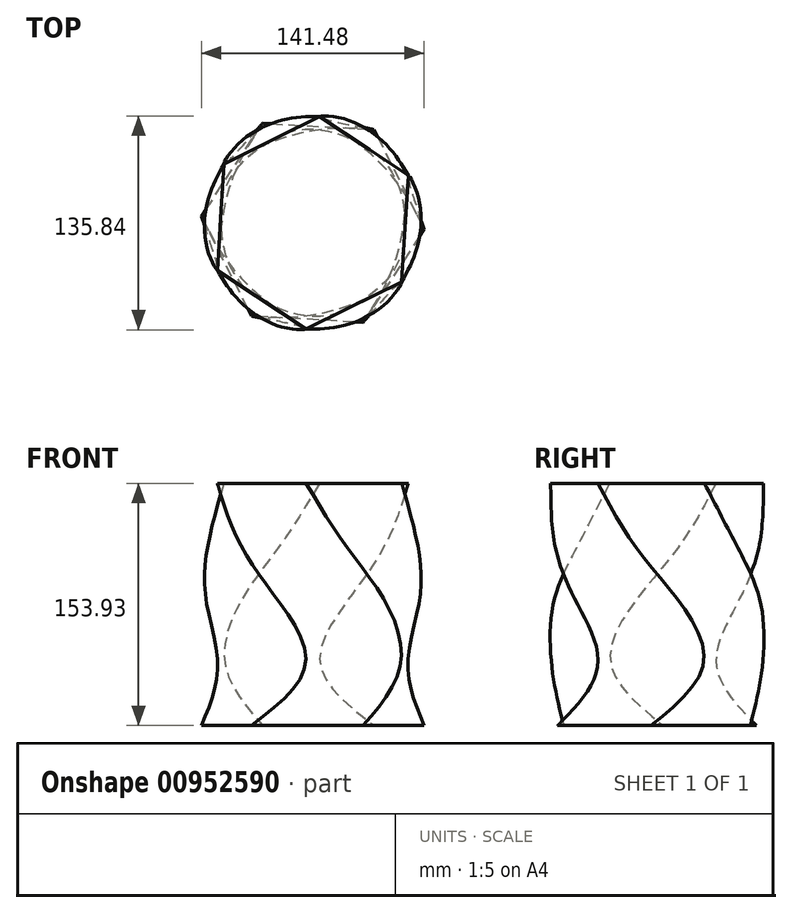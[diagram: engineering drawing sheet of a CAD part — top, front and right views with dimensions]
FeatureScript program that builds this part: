
annotation { "Feature Type Name" : "Feature", "Feature Type Description" : "" }
export const myFeature = defineFeature(function(context is Context, id is Id, definition is map)
    precondition{}
    {
        {
            var Q0;
            Q0=qCreatedBy(makeId("Top.planeOp"),FACE);
            cPlane(context, id + "F0", {"entities" : qUnion([Q0]), "cplaneType" : CPlaneType.OFFSET, "offset" : 77.22 * mm, "width" : 152.4 * mm, "height" : 152.4 * mm});
        }
        {
            var Q0;
            Q0=qCreatedBy(makeId("Top.planeOp"),FACE);
            cPlane(context, id + "F1", {"entities" : qUnion([Q0]), "cplaneType" : CPlaneType.OFFSET, "offset" : 38.1 * mm, "width" : 152.4 * mm, "height" : 152.4 * mm});
        }
        {
            var Q0;
            Q0=qCreatedBy(makeId("Top.planeOp"),FACE);
            cPlane(context, id + "F2", {"entities" : qUnion([Q0]), "cplaneType" : CPlaneType.OFFSET, "offset" : 76.7 * mm, "oppositeDirection" : true, "width" : 152.4 * mm, "height" : 152.4 * mm});
        }
        {
            var Q0;
            Q0=qCreatedBy(makeId("Top.planeOp"),FACE);
            cPlane(context, id + "F3", {"entities" : qUnion([Q0]), "cplaneType" : CPlaneType.OFFSET, "offset" : 34.54 * mm, "oppositeDirection" : true, "width" : 152.4 * mm, "height" : 152.4 * mm});
        }
        {
            var Q0;
            Q0=qCreatedBy(id+"F0.planeOp",FACE);
            var sketch = newSketch(context, id + "F4", { "sketchPlane" : qUnion([Q0])});
            skCircle(sketch, "E0.cCircle", {"center": v(0, 0) * mm, "radius": 58.65 * mm, "construction": true});
            skLineSegment(sketch, "E0.0", {"start": v(-56.43, 37.44) * mm, "end": v(4.21, 67.6) * mm});
            skLineSegment(sketch, "E0.1", {"start": v(4.21, 67.6) * mm, "end": v(60.64, 30.15) * mm});
            skLineSegment(sketch, "E0.2", {"start": v(60.64, 30.15) * mm, "end": v(56.43, -37.44) * mm});
            skLineSegment(sketch, "E0.3", {"start": v(56.43, -37.44) * mm, "end": v(-4.21, -67.6) * mm});
            skLineSegment(sketch, "E0.4", {"start": v(-4.21, -67.6) * mm, "end": v(-60.64, -30.15) * mm});
            skLineSegment(sketch, "E0.5", {"start": v(-60.64, -30.15) * mm, "end": v(-56.43, 37.44) * mm});
            skPoint(sketch, "E0.0.midPoint", {"position": v(-26.11, 52.52) * mm});
            skSolve(sketch);
        }
        {
            var Q0;
            Q0=qCreatedBy(id+"F1.planeOp",FACE);
            var sketch = newSketch(context, id + "F5", { "sketchPlane" : qUnion([Q0])});
            skCircle(sketch, "E1.cCircle", {"center": v(0, 0) * mm, "radius": 59.02 * mm, "construction": true});
            skLineSegment(sketch, "E1.0", {"start": v(45.97, 50.32) * mm, "end": v(66.56, -14.65) * mm});
            skLineSegment(sketch, "E1.1", {"start": v(66.56, -14.65) * mm, "end": v(20.6, -64.97) * mm});
            skLineSegment(sketch, "E1.2", {"start": v(20.6, -64.97) * mm, "end": v(-45.97, -50.32) * mm});
            skLineSegment(sketch, "E1.3", {"start": v(-45.97, -50.32) * mm, "end": v(-66.56, 14.65) * mm});
            skLineSegment(sketch, "E1.4", {"start": v(-66.56, 14.65) * mm, "end": v(-20.6, 64.97) * mm});
            skLineSegment(sketch, "E1.5", {"start": v(-20.6, 64.97) * mm, "end": v(45.97, 50.32) * mm});
            skPoint(sketch, "E1.0.midPoint", {"position": v(56.26, 17.83) * mm});
            skSolve(sketch);
        }
        {
            var Q0;
            Q0=qCreatedBy(makeId("Top.planeOp"),FACE);
            var sketch = newSketch(context, id + "F6", { "sketchPlane" : qUnion([Q0])});
            skCircle(sketch, "E2.cCircle", {"center": v(0, 0) * mm, "radius": 59.78 * mm, "construction": true});
            skLineSegment(sketch, "E2.0", {"start": v(-47.12, 50.44) * mm, "end": v(20.12, 66.03) * mm});
            skLineSegment(sketch, "E2.1", {"start": v(20.12, 66.03) * mm, "end": v(67.24, 15.59) * mm});
            skLineSegment(sketch, "E2.2", {"start": v(67.24, 15.59) * mm, "end": v(47.12, -50.44) * mm});
            skLineSegment(sketch, "E2.3", {"start": v(47.12, -50.44) * mm, "end": v(-20.12, -66.03) * mm});
            skLineSegment(sketch, "E2.4", {"start": v(-20.12, -66.03) * mm, "end": v(-67.24, -15.59) * mm});
            skLineSegment(sketch, "E2.5", {"start": v(-67.24, -15.59) * mm, "end": v(-47.12, 50.44) * mm});
            skPoint(sketch, "E2.0.midPoint", {"position": v(-13.5, 58.23) * mm});
            skSolve(sketch);
        }
        {
            var Q0;
            Q0=qCreatedBy(id+"F3.planeOp",FACE);
            var sketch = newSketch(context, id + "F7", { "sketchPlane" : qUnion([Q0])});
            skCircle(sketch, "E3.cCircle", {"center": v(0, 0) * mm, "radius": 58.4 * mm, "construction": true});
            skLineSegment(sketch, "E3.0", {"start": v(4.37, 67.3) * mm, "end": v(60.46, 29.86) * mm});
            skLineSegment(sketch, "E3.1", {"start": v(60.46, 29.86) * mm, "end": v(56.1, -37.43) * mm});
            skLineSegment(sketch, "E3.2", {"start": v(56.1, -37.43) * mm, "end": v(-4.37, -67.3) * mm});
            skLineSegment(sketch, "E3.3", {"start": v(-4.37, -67.3) * mm, "end": v(-60.46, -29.86) * mm});
            skLineSegment(sketch, "E3.4", {"start": v(-60.46, -29.86) * mm, "end": v(-56.1, 37.43) * mm});
            skLineSegment(sketch, "E3.5", {"start": v(-56.1, 37.43) * mm, "end": v(4.37, 67.3) * mm});
            skPoint(sketch, "E3.0.midPoint", {"position": v(32.42, 48.58) * mm});
            skSolve(sketch);
        }
        {
            var Q0;
            Q0=qCreatedBy(id+"F2.planeOp",FACE);
            var sketch = newSketch(context, id + "F8", { "sketchPlane" : qUnion([Q0])});
            skCircle(sketch, "E4.cCircle", {"center": v(0, 0) * mm, "radius": 61.35 * mm, "construction": true});
            skLineSegment(sketch, "E4.0", {"start": v(70.74, -3.96) * mm, "end": v(31.94, -63.24) * mm});
            skLineSegment(sketch, "E4.1", {"start": v(31.94, -63.24) * mm, "end": v(-38.8, -59.28) * mm});
            skLineSegment(sketch, "E4.2", {"start": v(-38.8, -59.28) * mm, "end": v(-70.74, 3.96) * mm});
            skLineSegment(sketch, "E4.3", {"start": v(-70.74, 3.96) * mm, "end": v(-31.94, 63.24) * mm});
            skLineSegment(sketch, "E4.4", {"start": v(-31.94, 63.24) * mm, "end": v(38.8, 59.28) * mm});
            skLineSegment(sketch, "E4.5", {"start": v(38.8, 59.28) * mm, "end": v(70.74, -3.96) * mm});
            skPoint(sketch, "E4.0.midPoint", {"position": v(51.34, -33.6) * mm});
            skSolve(sketch);
        }
        {
            var Q0;
            Q0=makeQuery(id+"F4.imprint","IMPRINT",FACE,{"disambiguationData":[TD([[makeQuery(id+"F4.imprint","IMPRINT",EDGE,{"derivedFrom":sQuery(id+"F4.wireOp",EDGE,"E0.0")}),-1.0]])]});
            var Q1;
            Q1=makeQuery(id+"F5.imprint","IMPRINT",FACE,{"disambiguationData":[TD([[makeQuery(id+"F5.imprint","IMPRINT",EDGE,{"derivedFrom":sQuery(id+"F5.wireOp",EDGE,"E1.0")}),-1.0]])]});
            var Q2;
            Q2=makeQuery(id+"F6.imprint","IMPRINT",FACE,{"disambiguationData":[TD([[makeQuery(id+"F6.imprint","IMPRINT",EDGE,{"derivedFrom":sQuery(id+"F6.wireOp",EDGE,"E2.0")}),-1.0]])]});
            var Q3;
            Q3=makeQuery(id+"F7.imprint","IMPRINT",FACE,{"disambiguationData":[TD([[makeQuery(id+"F7.imprint","IMPRINT",EDGE,{"derivedFrom":sQuery(id+"F7.wireOp",EDGE,"E3.0")}),-1.0]])]});
            var Q4;
            Q4=makeQuery(id+"F8.imprint","IMPRINT",FACE,{"disambiguationData":[TD([[makeQuery(id+"F8.imprint","IMPRINT",EDGE,{"derivedFrom":sQuery(id+"F8.wireOp",EDGE,"E4.0")}),-1.0]])]});
            loft(context, id + "F9", {"sheetProfilesArray" : [{ "sheetProfileEntities" : qUnion([Q0]) }, { "sheetProfileEntities" : qUnion([Q1]) }, { "sheetProfileEntities" : qUnion([Q2]) }, { "sheetProfileEntities" : qUnion([Q3]) }, { "sheetProfileEntities" : qUnion([Q4]) }]});
        }
    });
